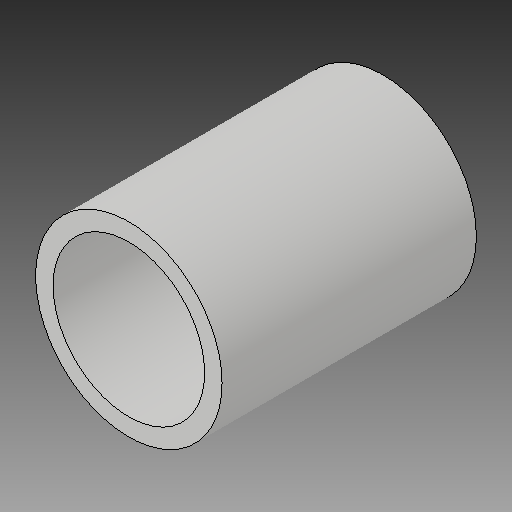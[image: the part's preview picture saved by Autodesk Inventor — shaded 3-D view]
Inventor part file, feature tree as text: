
AUTODESK INVENTOR PART (.ipt)
format: ipt  version: 2018 (Build 220112000, 112)  size: 101,888 bytes
history: native  units: in
note: dims shown in document units (in); Inventor stores cm internally (conversion verified against a paired STEP export)
features: other x3, sketch x1
ambient origin geometry x8: Origin, YZ Plane, XZ Plane, XY Plane, X Axis, Y Axis, Z Axis, Center Point
bodies: Solid1 (feature_tree)
feature tree (4):
  other  "terminal.ipt"
  other  "Solid1::terminal.ipt"
  other  "TaggingFeature1"
  sketch  "Sketch1"  dims[d0=0.3937in]
